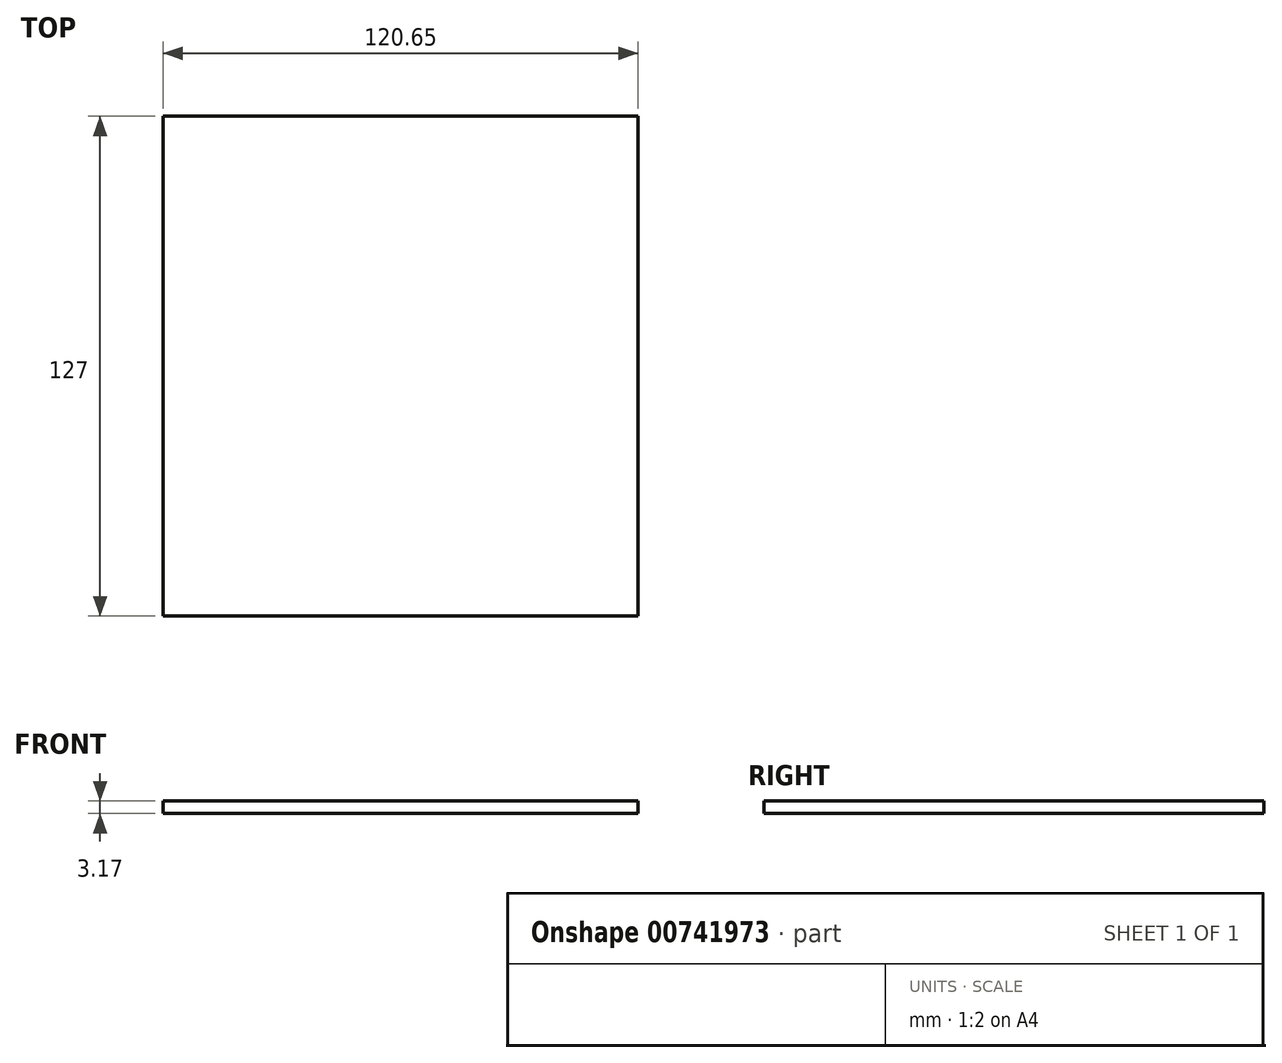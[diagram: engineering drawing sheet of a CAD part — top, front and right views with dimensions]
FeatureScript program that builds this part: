
annotation { "Feature Type Name" : "Feature", "Feature Type Description" : "" }
export const myFeature = defineFeature(function(context is Context, id is Id, definition is map)
    precondition{}
    {
        {
            var Q0;
            Q0=qCreatedBy(makeId("Top.planeOp"),FACE);
            var sketch = newSketch(context, id + "F0", { "sketchPlane" : qUnion([Q0])});
            skLineSegment(sketch, "E0.bottom", {"start": v(-72.24, 85.55) * mm, "end": v(48.41, 85.55) * mm});
            skLineSegment(sketch, "E0.top", {"start": v(-72.24, -41.45) * mm, "end": v(48.41, -41.45) * mm});
            skLineSegment(sketch, "E0.left", {"start": v(-72.24, 85.55) * mm, "end": v(-72.24, -41.45) * mm});
            skLineSegment(sketch, "E0.right", {"start": v(48.41, 85.55) * mm, "end": v(48.41, -41.45) * mm});
            skSolve(sketch);
        }
        {
            var Q0;
            Q0 = qSketchRegion(id + "F0", true);
            extrude(context, id + "F1", {"entities" : qUnion([Q0]), "depth" : 3.17 * mm, "offsetDistance" : 25.4 * mm});
        }
    });
